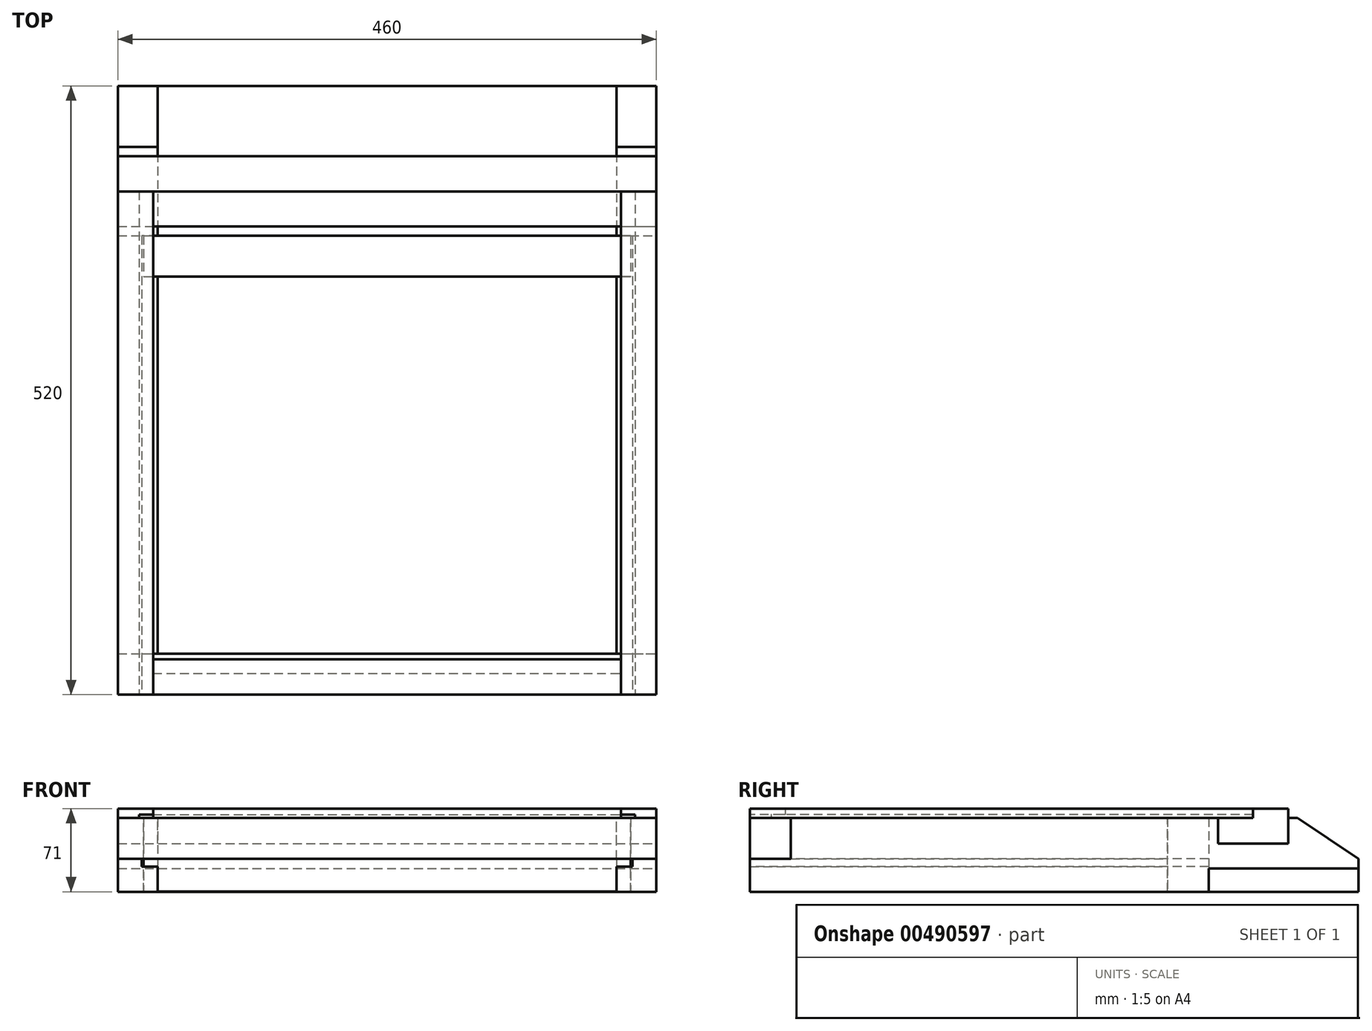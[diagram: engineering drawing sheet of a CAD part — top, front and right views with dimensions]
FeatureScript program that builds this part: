
annotation { "Feature Type Name" : "Feature", "Feature Type Description" : "" }
export const myFeature = defineFeature(function(context is Context, id is Id, definition is map)
    precondition{}
    {
        {
            var Q0;
            Q0=qCreatedBy(makeId("Top.planeOp"),FACE);
            var sketch = newSketch(context, id + "F0", { "sketchPlane" : qUnion([Q0])});
            skLineSegment(sketch, "E0.bottom", {"start": v(-196, 0) * mm, "end": v(-230, 0) * mm});
            skLineSegment(sketch, "E0.top", {"start": v(-196, -520) * mm, "end": v(-230, -520) * mm});
            skLineSegment(sketch, "E0.left", {"start": v(-196, 0) * mm, "end": v(-196, -520) * mm});
            skLineSegment(sketch, "E0.right", {"start": v(-230, 0) * mm, "end": v(-230, -520) * mm});
            skLineSegment(sketch, "E1.MirrorCS", {"start": v(196, -520) * mm, "end": v(230, -520) * mm});
            skLineSegment(sketch, "E2.MirrorCS", {"start": v(196, 0) * mm, "end": v(230, 0) * mm});
            skLineSegment(sketch, "E3.MirrorCS", {"start": v(196, 0) * mm, "end": v(196, -520) * mm});
            skLineSegment(sketch, "E4.MirrorCS", {"start": v(230, 0) * mm, "end": v(230, -520) * mm});
            skSolve(sketch);
        }
        {
            var Q0;
            Q0 = qSketchRegion(id + "F0", true);
            extrude(context, id + "F1", {"entities" : qUnion([Q0]), "depth" : 63 * mm, "offsetDistance" : 25 * mm});
        }
        {
            var Q0;
            Q0=makeQuery(id+"F1.opExtrude","SWEPT_FACE",FACE,{"disambiguationData":[OSD([sQuery(id+"F0.wireOp",EDGE,"E4.MirrorCS")])]});
            var sketch = newSketch(context, id + "F2", { "sketchPlane" : qUnion([Q0])});
            skLineSegment(sketch, "E5.0", {"start": v(-485, 28) * mm, "end": v(-485, 63) * mm});
            skLineSegment(sketch, "E5.1", {"start": v(-485, 28) * mm, "end": v(-520, 28) * mm});
            skLineSegment(sketch, "E5.2", {"start": v(-520, 28) * mm, "end": v(-520, 63) * mm});
            skLineSegment(sketch, "E5.3", {"start": v(-485, 63) * mm, "end": v(-520, 63) * mm});
            skLineSegment(sketch, "E6.1", {"start": v(-120, 41) * mm, "end": v(-60, 41) * mm});
            skLineSegment(sketch, "E6.2", {"start": v(-60, 41) * mm, "end": v(-60, 63) * mm});
            skLineSegment(sketch, "E6.3", {"start": v(-120, 41) * mm, "end": v(-120, 63) * mm});
            skLineSegment(sketch, "E6.4", {"start": v(-120, 63) * mm, "end": v(-60, 63) * mm});
            skLineSegment(sketch, "E6.5", {"start": v(0, 0) * mm, "end": v(-127.99, 0) * mm});
            skLineSegment(sketch, "E6.6", {"start": v(0, 20) * mm, "end": v(-127.99, 20) * mm});
            skLineSegment(sketch, "E6.7", {"start": v(0, 0) * mm, "end": v(0, 20) * mm});
            skLineSegment(sketch, "E7", {"start": v(-127.99, 20) * mm, "end": v(-127.99, 0) * mm});
            skLineSegment(sketch, "E8", {"start": v(-52, 63) * mm, "end": v(0, 28) * mm});
            skLineSegment(sketch, "E9", {"start": v(0, 28) * mm, "end": v(7.84, 28) * mm});
            skLineSegment(sketch, "E10", {"start": v(7.84, 28) * mm, "end": v(7.84, 69.2) * mm});
            skLineSegment(sketch, "E11", {"start": v(7.84, 69.2) * mm, "end": v(-52, 69.2) * mm});
            skLineSegment(sketch, "E12", {"start": v(-52, 69.2) * mm, "end": v(-52, 63) * mm});
            skSolve(sketch);
        }
        {
            var Q0;
            Q0 = qSketchRegion(id + "F2", true);
            extrude(context, id + "F3", {"entities" : qUnion([Q0]), "operationType" : NewBodyOperationType.REMOVE, "endBound" : BoundingType.THROUGH_ALL, "oppositeDirection" : true, "depth" : 25 * mm, "offsetDistance" : 25 * mm});
        }
        {
            var Q0;
            Q0=qCreatedBy(makeId("Right.planeOp"),FACE);
            var sketch = newSketch(context, id + "F4", { "sketchPlane" : qUnion([Q0])});
            skLineSegment(sketch, "E13.bottom", {"start": v(-90, 63) * mm, "end": v(-120, 63) * mm});
            skLineSegment(sketch, "E13.top", {"start": v(-60, 41) * mm, "end": v(-120, 41) * mm});
            skLineSegment(sketch, "E13.left", {"start": v(-60, 71) * mm, "end": v(-60, 41) * mm});
            skLineSegment(sketch, "E13.right", {"start": v(-120, 63) * mm, "end": v(-120, 41) * mm});
            skLineSegment(sketch, "E14.bottom", {"start": v(-520, 63) * mm, "end": v(-485, 63) * mm});
            skLineSegment(sketch, "E14.top", {"start": v(-520, 28) * mm, "end": v(-485, 28) * mm});
            skLineSegment(sketch, "E14.left", {"start": v(-520, 63) * mm, "end": v(-520, 28) * mm});
            skLineSegment(sketch, "E14.right", {"start": v(-485, 63) * mm, "end": v(-485, 28) * mm});
            skLineSegment(sketch, "E15.bottom", {"start": v(-127.99, 20) * mm, "end": v(0, 20) * mm});
            skLineSegment(sketch, "E15.top", {"start": v(-127.99, 0) * mm, "end": v(0, 0) * mm});
            skLineSegment(sketch, "E15.right", {"start": v(0, 20) * mm, "end": v(0, 0) * mm});
            skLineSegment(sketch, "E16", {"start": v(-127.99, 20) * mm, "end": v(-127.99, 0) * mm});
            skLineSegment(sketch, "E17", {"start": v(-90, 71) * mm, "end": v(-60, 71) * mm});
            skLineSegment(sketch, "E18", {"start": v(-90, 71) * mm, "end": v(-90, 63) * mm});
            skSolve(sketch);
        }
        {
            var Q0;
            Q0 = qSketchRegion(id + "F4", true);
            var Q1;
            Q1=makeQuery(id+"F1.opExtrude","SWEPT_FACE",FACE,{"disambiguationData":[OSD([sQuery(id+"F0.wireOp",EDGE,"E0.right")])]});
            var Q2;
            Q2=makeQuery(id+"F1.opExtrude","SWEPT_FACE",FACE,{"disambiguationData":[OSD([sQuery(id+"F0.wireOp",EDGE,"E4.MirrorCS")])]});
            extrude(context, id + "F5", {"entities" : qUnion([Q0]), "endBound" : BoundingType.UP_TO_SURFACE, "oppositeDirection" : true, "depth" : 25 * mm, "endBoundEntityFace" : qUnion([Q1]), "offsetDistance" : 25 * mm, "hasSecondDirection" : true, "secondDirectionBound" : BoundingType.UP_TO_SURFACE, "secondDirectionOppositeDirection" : false, "secondDirectionDepth" : 25 * mm, "secondDirectionBoundEntityFace" : qUnion([Q2])});
        }
        {
            var Q0;
            Q0=makeQuery(id+"F1.opExtrude","SWEPT_FACE",FACE,{"disambiguationData":[OSD([sQuery(id+"F0.wireOp",EDGE,"E1.MirrorCS")])]});
            var sketch = newSketch(context, id + "F6", { "sketchPlane" : qUnion([Q0])});
            skLineSegment(sketch, "E19.bottom", {"start": v(-209.61, 28) * mm, "end": v(-166.74, 28) * mm});
            skLineSegment(sketch, "E19.top", {"start": v(-209.61, 21.5) * mm, "end": v(-166.74, 21.5) * mm});
            skLineSegment(sketch, "E19.left", {"start": v(-209.61, 28) * mm, "end": v(-209.61, 21.5) * mm});
            skLineSegment(sketch, "E19.right", {"start": v(-166.74, 28) * mm, "end": v(-166.74, 21.5) * mm});
            skLineSegment(sketch, "E20.MirrorCS", {"start": v(209.61, 28) * mm, "end": v(209.61, 21.5) * mm});
            skLineSegment(sketch, "E21.MirrorCS", {"start": v(166.74, 28) * mm, "end": v(166.74, 21.5) * mm});
            skLineSegment(sketch, "E22.MirrorCS", {"start": v(209.61, 21.5) * mm, "end": v(166.74, 21.5) * mm});
            skLineSegment(sketch, "E23.MirrorCS", {"start": v(209.61, 28) * mm, "end": v(166.74, 28) * mm});
            skSolve(sketch);
        }
        {
            var Q0;
            Q0 = qSketchRegion(id + "F6", true);
            var Q1;
            Q1=makeQuery(id+"F5.opExtrude","SWEPT_FACE",FACE,{"disambiguationData":[OSD([sQuery(id+"F4.wireOp",EDGE,"E16")])]});
            extrude(context, id + "F7", {"entities" : qUnion([Q0]), "operationType" : NewBodyOperationType.REMOVE, "endBound" : BoundingType.UP_TO_SURFACE, "oppositeDirection" : true, "depth" : 25 * mm, "endBoundEntityFace" : qUnion([Q1]), "offsetDistance" : 25 * mm});
        }
        {
            var Q0;
            {var subQ0=sQuery(id+"F0.wireOp",EDGE,"E3.MirrorCS");var subQ1=sQuery(id+"F0.wireOp",EDGE,"E4.MirrorCS");Q0=makeQuery(id+"F3.boolean.opBoolean","SPLIT",FACE,{"disambiguationData":[TD([makeQuery(id+"F3.opExtrude","SWEPT_FACE",FACE,{"disambiguationData":[OSD([sQuery(id+"F2.wireOp",EDGE,"E5.0")])]})])],"derivedFrom":makeQuery(id+"F1.opExtrude","CAP_FACE",FACE,{"disambiguationData":[OSD([sQuery(id+"F0.wireOp",EDGE,"E1.MirrorCS"),sQuery(id+"F0.wireOp",EDGE,"E2.MirrorCS"),subQ0,subQ1])],"isStart":false})});}
            var sketch = newSketch(context, id + "F8", { "sketchPlane" : qUnion([Q0])});
            skLineSegment(sketch, "E24.0", {"start": v(-208, -163) * mm, "end": v(-182.5, -163) * mm});
            skLineSegment(sketch, "E24.1", {"start": v(-208, -128) * mm, "end": v(-182.5, -128) * mm});
            skLineSegment(sketch, "E25", {"start": v(-208, -163) * mm, "end": v(-208, -128) * mm});
            skPoint(sketch, "E26.orphan", {"position": v(-196, -163) * mm});
            skPoint(sketch, "E27.orphan", {"position": v(-196, -128) * mm});
            skLineSegment(sketch, "E28", {"start": v(-182.5, -163) * mm, "end": v(-182.5, -128) * mm});
            skPoint(sketch, "E29.orphan", {"position": v(188, -163) * mm});
            skPoint(sketch, "E30.orphan", {"position": v(188, -128) * mm});
            skLineSegment(sketch, "E31.MirrorCS", {"start": v(208, -128) * mm, "end": v(182.5, -128) * mm});
            skLineSegment(sketch, "E32.MirrorCS", {"start": v(208, -163) * mm, "end": v(182.5, -163) * mm});
            skPoint(sketch, "E33.MirrorP", {"position": v(196, -128) * mm});
            skLineSegment(sketch, "E34.MirrorCS", {"start": v(182.5, -163) * mm, "end": v(182.5, -128) * mm});
            skPoint(sketch, "E35.MirrorP", {"position": v(196, -163) * mm});
            skLineSegment(sketch, "E36.MirrorCS", {"start": v(208, -163) * mm, "end": v(208, -128) * mm});
            skSolve(sketch);
        }
        {
            var Q0;
            Q0 = qSketchRegion(id + "F8", true);
            extrude(context, id + "F9", {"entities" : qUnion([Q0]), "operationType" : NewBodyOperationType.REMOVE, "endBound" : BoundingType.THROUGH_ALL, "oppositeDirection" : true, "depth" : 25 * mm, "offsetDistance" : 25 * mm});
        }
        {
            var Q0;
            Q0=qCreatedBy(makeId("Right.planeOp"),FACE);
            var sketch = newSketch(context, id + "F10", { "sketchPlane" : qUnion([Q0])});
            skLineSegment(sketch, "E37.0.0", {"start": v(-163, 0.07) * mm, "end": v(-128, 0) * mm});
            skLineSegment(sketch, "E37.0.1", {"start": v(-128, 0) * mm, "end": v(-128, 63.07) * mm});
            skLineSegment(sketch, "E37.0.2", {"start": v(-128, 63.07) * mm, "end": v(-163, 63.07) * mm});
            skLineSegment(sketch, "E37.0.3", {"start": v(-163, 63.07) * mm, "end": v(-163, 0.07) * mm});
            skSolve(sketch);
        }
        {
            var Q0;
            Q0 = qSketchRegion(id + "F10", true);
            var Q1;
            Q1=makeQuery(id+"F9.boolean.opBoolean","COPY",FACE,{"derivedFrom":makeQuery(id+"F9.opExtrude","SWEPT_FACE",FACE,{"disambiguationData":[OSD([sQuery(id+"F8.wireOp",EDGE,"E25")])]})});
            var Q2;
            Q2=makeQuery(id+"F9.boolean.opBoolean","COPY",FACE,{"derivedFrom":makeQuery(id+"F9.opExtrude","SWEPT_FACE",FACE,{"disambiguationData":[OSD([sQuery(id+"F8.wireOp",EDGE,"E36.MirrorCS")])]})});
            extrude(context, id + "F11", {"entities" : qUnion([Q0]), "endBound" : BoundingType.UP_TO_SURFACE, "oppositeDirection" : true, "depth" : 25 * mm, "endBoundEntityFace" : qUnion([Q1]), "offsetDistance" : 25 * mm, "hasSecondDirection" : true, "secondDirectionBound" : BoundingType.UP_TO_SURFACE, "secondDirectionOppositeDirection" : false, "secondDirectionDepth" : 25 * mm, "secondDirectionBoundEntityFace" : qUnion([Q2])});
        }
        {
            var Q0;
            Q0=makeQuery(id+"F5.opExtrude","SWEPT_FACE",FACE,{"disambiguationData":[OSD([sQuery(id+"F4.wireOp",EDGE,"E14.left")])]});
            var sketch = newSketch(context, id + "F12", { "sketchPlane" : qUnion([Q0])});
            skLineSegment(sketch, "E38", {"start": v(230, 63) * mm, "end": v(230, 71) * mm});
            skLineSegment(sketch, "E39", {"start": v(230, 71) * mm, "end": v(200, 71) * mm});
            skLineSegment(sketch, "E40", {"start": v(200, 71) * mm, "end": v(200, 66) * mm});
            skLineSegment(sketch, "E41", {"start": v(200, 66) * mm, "end": v(212, 66) * mm});
            skLineSegment(sketch, "E42", {"start": v(212, 66) * mm, "end": v(212, 63) * mm});
            skLineSegment(sketch, "E43", {"start": v(212, 63) * mm, "end": v(230, 63) * mm});
            skLineSegment(sketch, "E44.MirrorCS", {"start": v(-200, 66) * mm, "end": v(-212, 66) * mm});
            skLineSegment(sketch, "E45.MirrorCS", {"start": v(-230, 63) * mm, "end": v(-230, 71) * mm});
            skLineSegment(sketch, "E46.MirrorCS", {"start": v(-200, 71) * mm, "end": v(-200, 66) * mm});
            skLineSegment(sketch, "E47.MirrorCS", {"start": v(-212, 66) * mm, "end": v(-212, 63) * mm});
            skLineSegment(sketch, "E48.MirrorCS", {"start": v(-230, 71) * mm, "end": v(-200, 71) * mm});
            skLineSegment(sketch, "E49.MirrorCS", {"start": v(-212, 63) * mm, "end": v(-230, 63) * mm});
            skSolve(sketch);
        }
        {
            var Q0;
            Q0 = qSketchRegion(id + "F12", true);
            var Q1;
            Q1=makeQuery(id+"F5.opExtrude","SWEPT_FACE",FACE,{"disambiguationData":[OSD([sQuery(id+"F4.wireOp",EDGE,"E18")])]});
            extrude(context, id + "F13", {"entities" : qUnion([Q0]), "endBound" : BoundingType.UP_TO_SURFACE, "oppositeDirection" : true, "depth" : 25 * mm, "endBoundEntityFace" : qUnion([Q1]), "offsetDistance" : 25 * mm});
        }
        {
            var Q0;
            Q0=makeQuery(id+"F13.opExtrude","SWEPT_FACE",FACE,{"disambiguationData":[OSD([sQuery(id+"F12.wireOp",EDGE,"E40")])]});
            var sketch = newSketch(context, id + "F14", { "sketchPlane" : qUnion([Q0])});
            skLineSegment(sketch, "E50", {"start": v(519.93, 63) * mm, "end": v(519.93, 71) * mm});
            skLineSegment(sketch, "E51", {"start": v(519.93, 71) * mm, "end": v(489.93, 71) * mm});
            skLineSegment(sketch, "E52", {"start": v(489.93, 71) * mm, "end": v(489.93, 66) * mm});
            skLineSegment(sketch, "E53", {"start": v(489.93, 66) * mm, "end": v(501.93, 66) * mm});
            skLineSegment(sketch, "E54", {"start": v(501.93, 66) * mm, "end": v(501.93, 63) * mm});
            skLineSegment(sketch, "E55", {"start": v(501.93, 63) * mm, "end": v(519.93, 63) * mm});
            skSolve(sketch);
        }
        {
            var Q0;
            Q0 = qSketchRegion(id + "F14", true);
            var Q1;
            Q1=makeQuery(id+"F13.opExtrude","SWEPT_FACE",FACE,{"disambiguationData":[OSD([sQuery(id+"F12.wireOp",EDGE,"E46.MirrorCS")])]});
            extrude(context, id + "F15", {"entities" : qUnion([Q0]), "endBound" : BoundingType.UP_TO_SURFACE, "depth" : 25 * mm, "endBoundEntityFace" : qUnion([Q1]), "offsetDistance" : 25 * mm});
        }
    });
